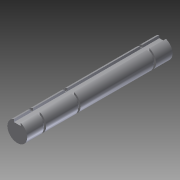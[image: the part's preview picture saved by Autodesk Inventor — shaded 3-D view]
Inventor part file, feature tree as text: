
AUTODESK INVENTOR PART (.ipt)
format: ipt  version: 2012 (Build 160160000, 160)  size: 115,200 bytes
history: native  units: in
note: dims shown in document units (in); Inventor stores cm internally (conversion verified against a paired STEP export)
features: extrude x5, sketch x4, plane x4
ambient origin geometry x8: Origin, YZ Plane, XZ Plane, XY Plane, X Axis, Y Axis, Z Axis, Center Point
bodies: Solid1 (feature_tree)
feature tree (13):
  sketch  "Sketch1"  dims[d0=0.375in d1=2.75in d2=0.0in]
  extrude  "Extrusion1"  Depth=2.75in TaperAngle=0.0deg
  plane  "Work Plane1"
  extrude  "Extrusion2"  Depth=0.045in TaperAngle=0.0deg
  plane  "Work Plane2"
  extrude  "Extrusion3"  [1 undecoded]
  plane  "Work Plane3"
  extrude  "Extrusion4"  [1 undecoded]
  plane  "Work Plane4"
  extrude  "Extrusion6"  Depth=0.125in
  sketch  "Sketch2"  dims[d4=0.3in d5=0.045in d6=0.0in]
  sketch  "Sketch3"  dims[d8=0.045in d9=0.0in d10=-1.009in]
  sketch  "Sketch4"  dims[d11=0.045in d12=0.0in d13=-0.066in d16=0.125in d17=0.125in d18=0.0625in d19=0.25in d20=1.0in d21=0.0in d24=-0.3125in d25=-0.3125in]
note: 2 required parameter values undecoded (feature->parameter linkage not recoverable at this tier; creation-order binding heuristic only, values carry confidence <= 0.55)
